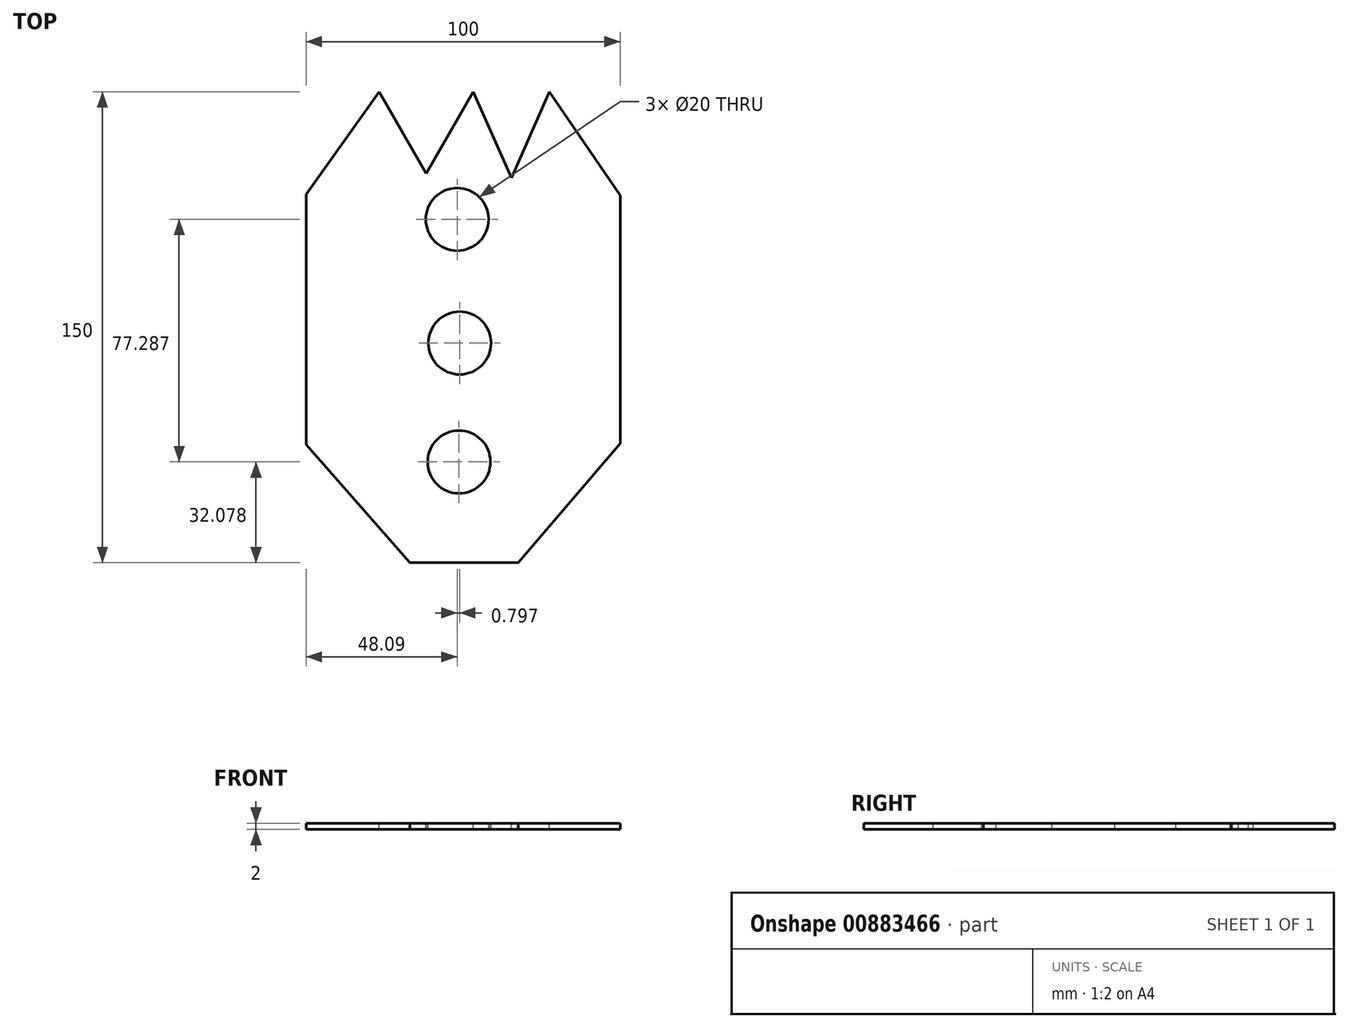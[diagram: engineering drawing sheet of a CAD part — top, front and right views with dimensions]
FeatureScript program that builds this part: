
annotation { "Feature Type Name" : "Feature", "Feature Type Description" : "" }
export const myFeature = defineFeature(function(context is Context, id is Id, definition is map)
    precondition{}
    {
        {
            var Q0;
            Q0=qCreatedBy(makeId("Top.planeOp"),FACE);
            var sketch = newSketch(context, id + "F0", { "sketchPlane" : qUnion([Q0])});
            skLineSegment(sketch, "E0.bottom", {"start": v(-58.16, 135.16) * mm, "end": v(41.84, 135.16) * mm});
            skLineSegment(sketch, "E0.top", {"start": v(-58.16, -14.84) * mm, "end": v(41.84, -14.84) * mm});
            skLineSegment(sketch, "E0.left", {"start": v(-58.16, 135.16) * mm, "end": v(-58.16, -14.84) * mm});
            skLineSegment(sketch, "E0.right", {"start": v(41.84, 135.16) * mm, "end": v(41.84, -14.84) * mm});
            skSolve(sketch);
        }
        {
            var Q0;
            Q0 = qSketchRegion(id + "F0", true);
            extrude(context, id + "F1", {"entities" : qUnion([Q0]), "depth" : 1 * mm, "offsetDistance" : 25 * mm});
        }
        {
            var Q0;
            Q0=makeQuery(id+"F1.opExtrude","CAP_FACE",FACE,{"disambiguationData":[OSD([sQuery(id+"F0.wireOp",EDGE,"E0.bottom"),sQuery(id+"F0.wireOp",EDGE,"E0.top"),sQuery(id+"F0.wireOp",EDGE,"E0.left"),sQuery(id+"F0.wireOp",EDGE,"E0.right")])],"isStart":false});
            var sketch = newSketch(context, id + "F2", { "sketchPlane" : qUnion([Q0])});
            skCircle(sketch, "E1", {"center": v(-10.07, 94.53) * mm, "radius": 10 * mm});
            skCircle(sketch, "E2", {"center": v(-9.5, 17.24) * mm, "radius": 10 * mm});
            skCircle(sketch, "E3", {"center": v(-9.27, 55.12) * mm, "radius": 10 * mm});
            skSolve(sketch);
        }
        {
            var Q0;
            Q0 = qSketchRegion(id + "F2", true);
            extrude(context, id + "F3", {"entities" : qUnion([Q0]), "operationType" : NewBodyOperationType.REMOVE, "oppositeDirection" : true, "depth" : 25 * mm, "offsetDistance" : 25 * mm});
        }
        {
            var Q0;
            Q0=makeQuery(id+"F1.opExtrude","CAP_FACE",FACE,{"disambiguationData":[OSD([sQuery(id+"F0.wireOp",EDGE,"E0.bottom"),sQuery(id+"F0.wireOp",EDGE,"E0.top"),sQuery(id+"F0.wireOp",EDGE,"E0.left"),sQuery(id+"F0.wireOp",EDGE,"E0.right")])],"isStart":false});
            var sketch = newSketch(context, id + "F4", { "sketchPlane" : qUnion([Q0])});
            skLineSegment(sketch, "E4", {"start": v(-58.16, 22.72) * mm, "end": v(-25.15, -14.84) * mm});
            skLineSegment(sketch, "E5", {"start": v(41.84, 23.2) * mm, "end": v(9.38, -14.84) * mm});
            skSolve(sketch);
        }
        {
            var Q0;
            {var subQ0=sQuery(id+"F4.wireOp",EDGE,"E5");Q0=makeQuery(id+"F4.imprint","IMPRINT",FACE,{"disambiguationData":[TD([[makeQuery(id+"F4.imprint","IMPRINT",EDGE,{"derivedFrom":subQ0}),1.0]])]});}
            var Q1;
            {var subQ0=sQuery(id+"F4.wireOp",EDGE,"E4");Q1=makeQuery(id+"F4.imprint","IMPRINT",FACE,{"disambiguationData":[TD([[makeQuery(id+"F4.imprint","IMPRINT",EDGE,{"derivedFrom":subQ0}),-1.0]])]});}
            var Q2;
            Q2=sQuery(id+"F4.wireOp",EDGE,"E5");
            extrude(context, id + "F5", {"entities" : qUnion([Q0, Q1]), "operationType" : NewBodyOperationType.REMOVE, "surfaceEntities" : qUnion([Q2]), "oppositeDirection" : true, "depth" : 25 * mm, "offsetDistance" : 25 * mm});
        }
        {
            var Q0;
            Q0=makeQuery(id+"F1.opExtrude","CAP_FACE",FACE,{"disambiguationData":[OSD([sQuery(id+"F0.wireOp",EDGE,"E0.bottom"),sQuery(id+"F0.wireOp",EDGE,"E0.top"),sQuery(id+"F0.wireOp",EDGE,"E0.left"),sQuery(id+"F0.wireOp",EDGE,"E0.right")])],"isStart":false});
            var sketch = newSketch(context, id + "F6", { "sketchPlane" : qUnion([Q0])});
            skLineSegment(sketch, "E6", {"start": v(-58.16, 102.57) * mm, "end": v(-34.97, 135.16) * mm});
            skLineSegment(sketch, "E7", {"start": v(-34.97, 135.16) * mm, "end": v(-19.96, 109.18) * mm});
            skLineSegment(sketch, "E8", {"start": v(-19.96, 109.18) * mm, "end": v(-4.96, 135.16) * mm});
            skLineSegment(sketch, "E9", {"start": v(-4.96, 135.16) * mm, "end": v(7.19, 107.73) * mm});
            skLineSegment(sketch, "E10", {"start": v(7.19, 107.73) * mm, "end": v(19.33, 135.16) * mm});
            skLineSegment(sketch, "E11", {"start": v(19.33, 135.16) * mm, "end": v(41.84, 102.1) * mm});
            skSolve(sketch);
        }
        {
            var Q0;
            {var subQ2=sQuery(id+"F6.wireOp",EDGE,"E6");Q0=makeQuery(id+"F6.imprint","IMPRINT",FACE,{"disambiguationData":[TD([[makeQuery(id+"F6.imprint","IMPRINT",EDGE,{"derivedFrom":subQ2}),-1.0]])]});}
            var sketch = newSketch(context, id + "F7", { "sketchPlane" : qUnion([Q0])});
            skSolve(sketch);
        }
        {
            var Q0;
            Q0 = qSketchRegion(id + "F7", true);
            var Q1;
            {var subQ0=sQuery(id+"F6.wireOp",EDGE,"E7");Q1=makeQuery(id+"F6.imprint","IMPRINT",FACE,{"disambiguationData":[TD([[makeQuery(id+"F6.imprint","IMPRINT",EDGE,{"derivedFrom":subQ0}),1.0]])]});}
            var Q2;
            {var subQ0=sQuery(id+"F6.wireOp",EDGE,"E9");Q2=makeQuery(id+"F6.imprint","IMPRINT",FACE,{"disambiguationData":[TD([[makeQuery(id+"F6.imprint","IMPRINT",EDGE,{"derivedFrom":subQ0}),1.0]])]});}
            var Q3;
            {var subQ0=sQuery(id+"F6.wireOp",EDGE,"E11");Q3=makeQuery(id+"F6.imprint","IMPRINT",FACE,{"disambiguationData":[TD([[makeQuery(id+"F6.imprint","IMPRINT",EDGE,{"derivedFrom":subQ0}),1.0]])]});}
            var Q4;
            {var subQ0=sQuery(id+"F6.wireOp",EDGE,"E6");Q4=makeQuery(id+"F6.imprint","IMPRINT",FACE,{"disambiguationData":[TD([[makeQuery(id+"F6.imprint","IMPRINT",EDGE,{"derivedFrom":subQ0}),1.0]])]});}
            extrude(context, id + "F8", {"entities" : qUnion([Q0, Q1, Q2, Q3, Q4]), "operationType" : NewBodyOperationType.REMOVE, "oppositeDirection" : true, "depth" : 25 * mm, "offsetDistance" : 25 * mm});
        }
        {
            var Q0;
            {var subQ2=sQuery(id+"F6.wireOp",EDGE,"E6");Q0=makeQuery(id+"F7.imprint","IMPRINT",FACE,{"disambiguationData":[TD([[makeQuery(id+"F7.imprint","IMPRINT",EDGE,{"derivedFrom":makeQuery(id+"F6.imprint","IMPRINT",EDGE,{"derivedFrom":subQ2})}),-1.0]])]});}
            extrude(context, id + "F9", {"entities" : qUnion([Q0]), "operationType" : NewBodyOperationType.ADD, "depth" : 1 * mm, "offsetDistance" : 25 * mm});
        }
    });
